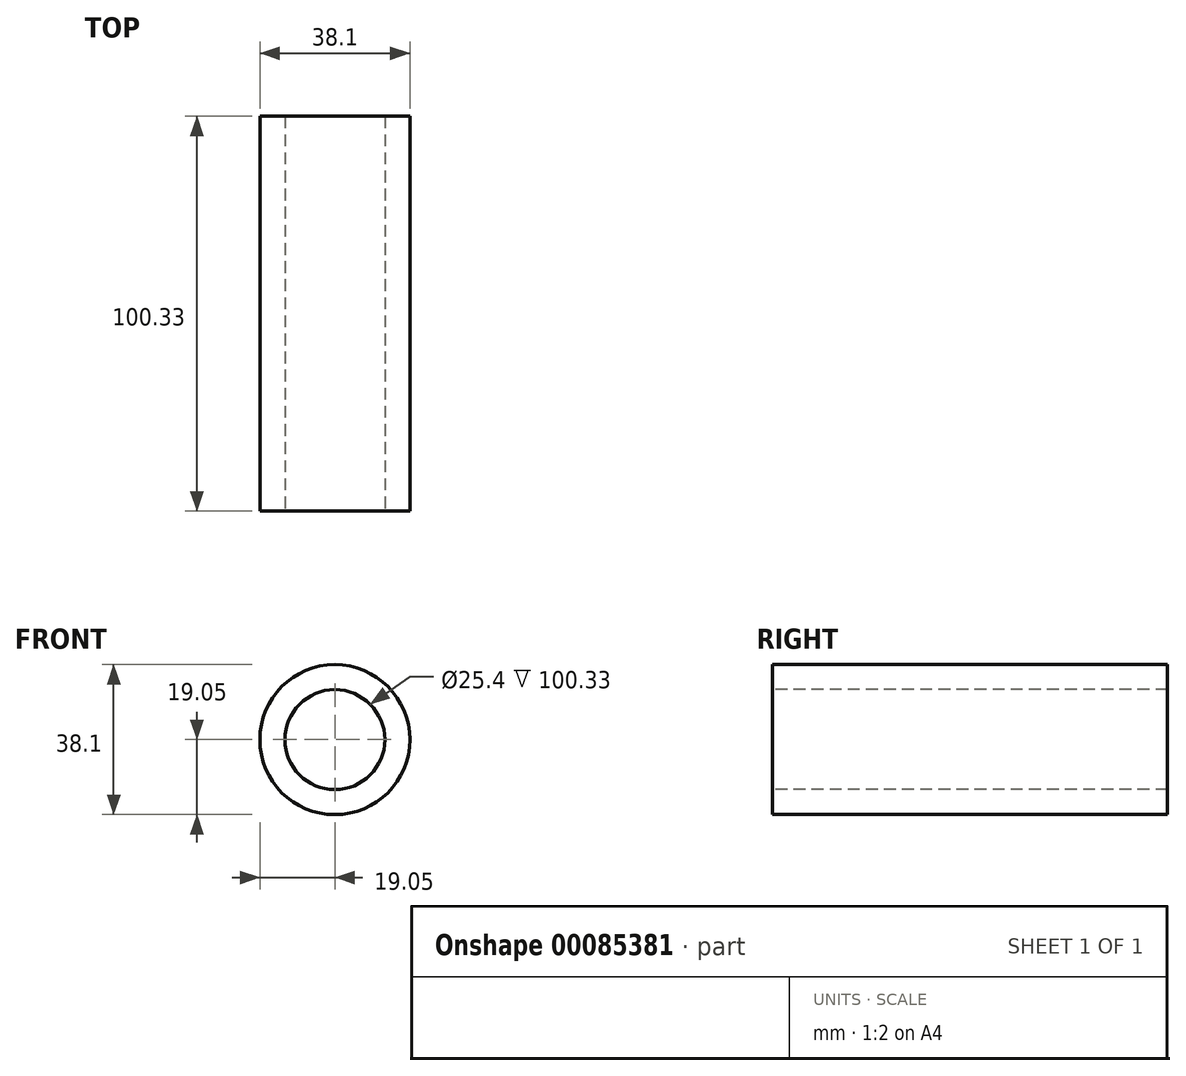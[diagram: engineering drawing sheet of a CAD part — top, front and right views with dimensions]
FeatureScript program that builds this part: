
annotation { "Feature Type Name" : "Feature", "Feature Type Description" : "" }
export const myFeature = defineFeature(function(context is Context, id is Id, definition is map)
    precondition{}
    {
        {
            var Q0;
            Q0=qCreatedBy(makeId("Right.planeOp"),FACE);
            var sketch = newSketch(context, id + "F0", { "sketchPlane" : qUnion([Q0])});
            skLineSegment(sketch, "E0.bottom", {"start": v(-100.33, 19.05) * mm, "end": v(0, 19.05) * mm});
            skLineSegment(sketch, "E0.top", {"start": v(-100.33, 0) * mm, "end": v(0, 0) * mm});
            skLineSegment(sketch, "E0.left", {"start": v(-100.33, 19.05) * mm, "end": v(-100.33, 0) * mm});
            skLineSegment(sketch, "E0.right", {"start": v(0, 19.05) * mm, "end": v(0, 0) * mm});
            skLineSegment(sketch, "E1.bottom", {"start": v(-100.33, 19.05) * mm, "end": v(-88.9, 19.05) * mm});
            skLineSegment(sketch, "E1.top", {"start": v(-96.52, 34.29) * mm, "end": v(-92.7, 34.29) * mm});
            skLineSegment(sketch, "E1.left", {"start": v(-100.33, 19.05) * mm, "end": v(-100.33, 30.48) * mm});
            skLineSegment(sketch, "E1.right", {"start": v(-88.9, 19.05) * mm, "end": v(-88.9, 30.48) * mm});
            skLineSegment(sketch, "E2.bottom", {"start": v(-82.55, 19.05) * mm, "end": v(-71.12, 19.05) * mm});
            skLineSegment(sketch, "E2.top", {"start": v(-78.74, 33.02) * mm, "end": v(-74.93, 33.02) * mm});
            skLineSegment(sketch, "E2.left", {"start": v(-82.55, 19.05) * mm, "end": v(-82.55, 29.2) * mm});
            skLineSegment(sketch, "E2.right", {"start": v(-71.12, 19.05) * mm, "end": v(-71.12, 29.2) * mm});
            skLineSegment(sketch, "E3.bottom", {"start": v(-64.77, 19.05) * mm, "end": v(-53.34, 19.05) * mm});
            skLineSegment(sketch, "E3.top", {"start": v(-60.96, 31.75) * mm, "end": v(-57.15, 31.75) * mm});
            skLineSegment(sketch, "E3.left", {"start": v(-64.77, 19.05) * mm, "end": v(-64.77, 27.94) * mm});
            skLineSegment(sketch, "E3.right", {"start": v(-53.34, 19.05) * mm, "end": v(-53.34, 27.94) * mm});
            skLineSegment(sketch, "E4.bottom", {"start": v(-46.99, 19.05) * mm, "end": v(-35.56, 19.05) * mm});
            skLineSegment(sketch, "E4.top", {"start": v(-43.18, 30.48) * mm, "end": v(-39.37, 30.48) * mm});
            skLineSegment(sketch, "E4.left", {"start": v(-46.99, 19.05) * mm, "end": v(-46.99, 26.67) * mm});
            skLineSegment(sketch, "E4.right", {"start": v(-35.56, 19.05) * mm, "end": v(-35.56, 26.67) * mm});
            skLineSegment(sketch, "E5.bottom", {"start": v(-29.2, 19.05) * mm, "end": v(-17.78, 19.05) * mm});
            skLineSegment(sketch, "E5.top", {"start": v(-25.4, 31.75) * mm, "end": v(-21.59, 31.75) * mm});
            skLineSegment(sketch, "E5.left", {"start": v(-29.2, 19.05) * mm, "end": v(-29.2, 27.94) * mm});
            skLineSegment(sketch, "E5.right", {"start": v(-17.78, 19.05) * mm, "end": v(-17.78, 27.94) * mm});
            skLineSegment(sketch, "E6.bottom", {"start": v(0, 19.05) * mm, "end": v(-11.43, 19.05) * mm});
            skLineSegment(sketch, "E6.top", {"start": v(-3.81, 33.02) * mm, "end": v(-7.62, 33.02) * mm});
            skLineSegment(sketch, "E6.left", {"start": v(0, 19.05) * mm, "end": v(0, 29.2) * mm});
            skLineSegment(sketch, "E6.right", {"start": v(-11.43, 19.05) * mm, "end": v(-11.43, 29.2) * mm});
            skPoint(sketch, "E7.visualSharp", {"position": v(-100.33, 34.29) * mm});
            skArc(sketch, "E7.filletArc", {"start": v(-96.52, 34.29) * mm, "mid": v(-99.21, 33.17) * mm, "end": v(-100.33, 30.48) * mm});
            skPoint(sketch, "E8.visualSharp", {"position": v(-88.9, 34.29) * mm});
            skArc(sketch, "E8.filletArc", {"start": v(-88.9, 30.48) * mm, "mid": v(-90.02, 33.17) * mm, "end": v(-92.7, 34.29) * mm});
            skPoint(sketch, "E9.visualSharp", {"position": v(-82.55, 33.02) * mm});
            skArc(sketch, "E9.filletArc", {"start": v(-78.74, 33.02) * mm, "mid": v(-81.43, 31.9) * mm, "end": v(-82.55, 29.2) * mm});
            skPoint(sketch, "E10.visualSharp", {"position": v(-71.12, 33.02) * mm});
            skArc(sketch, "E10.filletArc", {"start": v(-71.12, 29.2) * mm, "mid": v(-72.24, 31.9) * mm, "end": v(-74.93, 33.02) * mm});
            skPoint(sketch, "E11.visualSharp", {"position": v(-64.77, 31.75) * mm});
            skArc(sketch, "E11.filletArc", {"start": v(-60.96, 31.75) * mm, "mid": v(-63.65, 30.63) * mm, "end": v(-64.77, 27.94) * mm});
            skPoint(sketch, "E12.visualSharp", {"position": v(-53.34, 31.75) * mm});
            skArc(sketch, "E12.filletArc", {"start": v(-53.34, 27.94) * mm, "mid": v(-54.46, 30.63) * mm, "end": v(-57.15, 31.75) * mm});
            skPoint(sketch, "E13.visualSharp", {"position": v(-46.99, 30.48) * mm});
            skArc(sketch, "E13.filletArc", {"start": v(-43.18, 30.48) * mm, "mid": v(-45.87, 29.36) * mm, "end": v(-47, 26.67) * mm});
            skPoint(sketch, "E14.visualSharp", {"position": v(-35.56, 30.48) * mm});
            skArc(sketch, "E14.filletArc", {"start": v(-35.56, 26.67) * mm, "mid": v(-36.68, 29.36) * mm, "end": v(-39.37, 30.48) * mm});
            skPoint(sketch, "E15.visualSharp", {"position": v(-29.2, 31.75) * mm});
            skArc(sketch, "E15.filletArc", {"start": v(-25.4, 31.75) * mm, "mid": v(-28.1, 30.63) * mm, "end": v(-29.2, 27.94) * mm});
            skPoint(sketch, "E16.visualSharp", {"position": v(-17.78, 31.75) * mm});
            skArc(sketch, "E16.filletArc", {"start": v(-17.78, 27.94) * mm, "mid": v(-18.9, 30.63) * mm, "end": v(-21.59, 31.75) * mm});
            skPoint(sketch, "E17.visualSharp", {"position": v(-11.43, 33.02) * mm});
            skArc(sketch, "E17.filletArc", {"start": v(-7.62, 33.02) * mm, "mid": v(-10.31, 31.9) * mm, "end": v(-11.43, 29.2) * mm});
            skPoint(sketch, "E18.visualSharp", {"position": v(0, 33.02) * mm});
            skArc(sketch, "E18.filletArc", {"start": v(0, 29.2) * mm, "mid": v(-1.12, 31.9) * mm, "end": v(-3.81, 33.02) * mm});
            skSolve(sketch);
        }
        {
            var Q0;
            Q0=makeQuery(id+"F0.imprint","IMPRINT",FACE,{"disambiguationData":[TD([[makeQuery(id+"F0.imprint","IMPRINT",EDGE,{"derivedFrom":sQuery(id+"F0.wireOp",EDGE,"E1.bottom")}),1.0]])]});
            var Q1;
            Q1=makeQuery(id+"F0.imprint","IMPRINT",FACE,{"disambiguationData":[TD([[makeQuery(id+"F0.imprint","IMPRINT",EDGE,{"derivedFrom":sQuery(id+"F0.wireOp",EDGE,"E2.bottom")}),1.0]])]});
            var Q2;
            Q2=makeQuery(id+"F0.imprint","IMPRINT",FACE,{"disambiguationData":[TD([[makeQuery(id+"F0.imprint","IMPRINT",EDGE,{"derivedFrom":sQuery(id+"F0.wireOp",EDGE,"E3.bottom")}),1.0]])]});
            var Q3;
            Q3=makeQuery(id+"F0.imprint","IMPRINT",FACE,{"disambiguationData":[TD([[makeQuery(id+"F0.imprint","IMPRINT",EDGE,{"derivedFrom":sQuery(id+"F0.wireOp",EDGE,"E4.bottom")}),1.0]])]});
            var Q4;
            Q4=makeQuery(id+"F0.imprint","IMPRINT",FACE,{"disambiguationData":[TD([[makeQuery(id+"F0.imprint","IMPRINT",EDGE,{"derivedFrom":sQuery(id+"F0.wireOp",EDGE,"E5.bottom")}),1.0]])]});
            var Q5;
            Q5=makeQuery(id+"F0.imprint","IMPRINT",FACE,{"disambiguationData":[TD([[makeQuery(id+"F0.imprint","IMPRINT",EDGE,{"derivedFrom":sQuery(id+"F0.wireOp",EDGE,"E6.bottom")}),-1.0]])]});
            var Q6;
            Q6=makeQuery(id+"F0.imprint","IMPRINT",FACE,{"disambiguationData":[TD([[makeQuery(id+"F0.imprint","IMPRINT",EDGE,{"derivedFrom":sQuery(id+"F0.wireOp",EDGE,"E0.top")}),1.0]])]});
            var Q7;
            Q7=sQuery(id+"F0.wireOp",EDGE,"E0.top");
            revolve(context, id + "F1", {"entities" : qUnion([Q0, Q1, Q2, Q3, Q4, Q5, Q6]), "axis" : qUnion([Q7]), "revolveType" : RevolveType.FULL});
        }
        {
            var Q0;
            Q0=makeQuery(id+"F1.opRevolve","SWEPT_FACE",FACE,{"disambiguationData":[OSD([sQuery(id+"F0.wireOp",EDGE,"E0.left"),sQuery(id+"F0.wireOp",EDGE,"E1.left")])]});
            var sketch = newSketch(context, id + "F2", { "sketchPlane" : qUnion([Q0])});
            skCircle(sketch, "E19", {"center": v(0, 0) * mm, "radius": 12.7 * mm});
            skSolve(sketch);
        }
        {
            var Q0;
            Q0=makeQuery(id+"F2.imprint","IMPRINT",FACE,{"disambiguationData":[TD([[makeQuery(id+"F2.imprint","IMPRINT",EDGE,{"derivedFrom":sQuery(id+"F2.wireOp",EDGE,"E19")}),1.0]])]});
            extrude(context, id + "F3", {"entities" : qUnion([Q0]), "operationType" : NewBodyOperationType.REMOVE, "endBound" : BoundingType.THROUGH_ALL, "oppositeDirection" : true, "depth" : 101.6 * mm});
        }
    });
